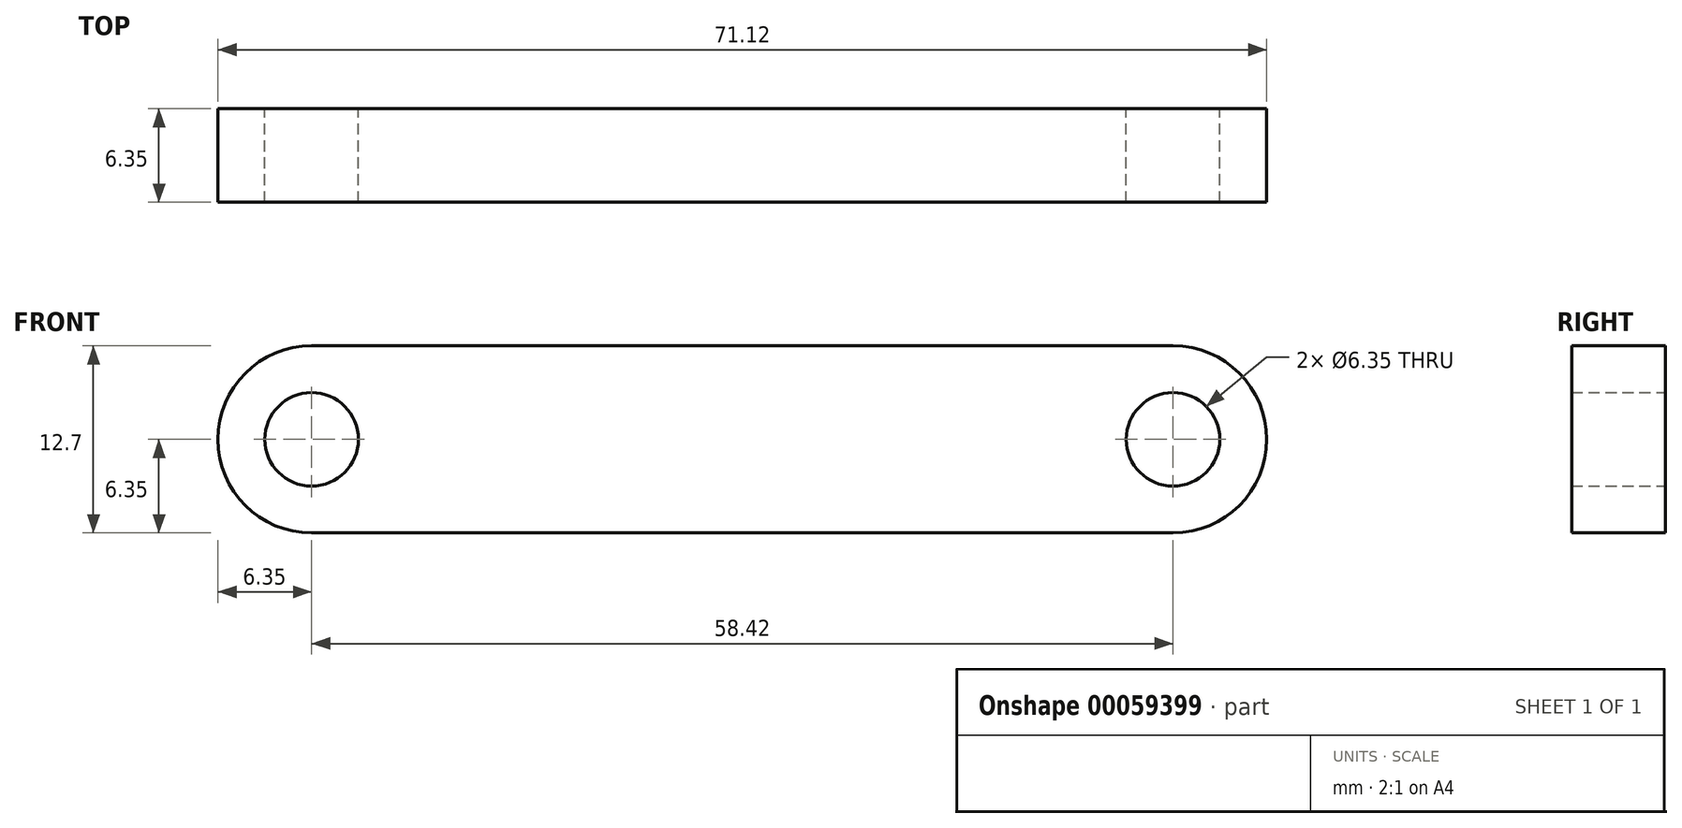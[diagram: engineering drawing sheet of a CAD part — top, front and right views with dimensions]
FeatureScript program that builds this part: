
annotation { "Feature Type Name" : "Feature", "Feature Type Description" : "" }
export const myFeature = defineFeature(function(context is Context, id is Id, definition is map)
    precondition{}
    {
        {
            var Q0;
            Q0=qCreatedBy(makeId("Front.planeOp"),FACE);
            var sketch = newSketch(context, id + "F0", { "sketchPlane" : qUnion([Q0])});
            skCircle(sketch, "E0", {"center": v(0, 0) * mm, "radius": 3.18 * mm});
            skArc(sketch, "E1", {"start": v(0, 6.35) * mm, "mid": v(-6.35, 0) * mm, "end": v(0, -6.35) * mm});
            skCircle(sketch, "E2", {"center": v(58.42, 0) * mm, "radius": 3.18 * mm});
            skArc(sketch, "E3", {"start": v(58.42, -6.35) * mm, "mid": v(64.77, 0) * mm, "end": v(58.42, 6.35) * mm});
            skLineSegment(sketch, "E4", {"start": v(0, -6.35) * mm, "end": v(58.42, -6.35) * mm});
            skLineSegment(sketch, "E5", {"start": v(58.42, 6.35) * mm, "end": v(0, 6.35) * mm});
            skSolve(sketch);
        }
        {
            var Q0;
            Q0 = qSketchRegion(id + "F0", true);
            extrude(context, id + "F1", {"entities" : qUnion([Q0]), "depth" : 6.35 * mm});
        }
    });
